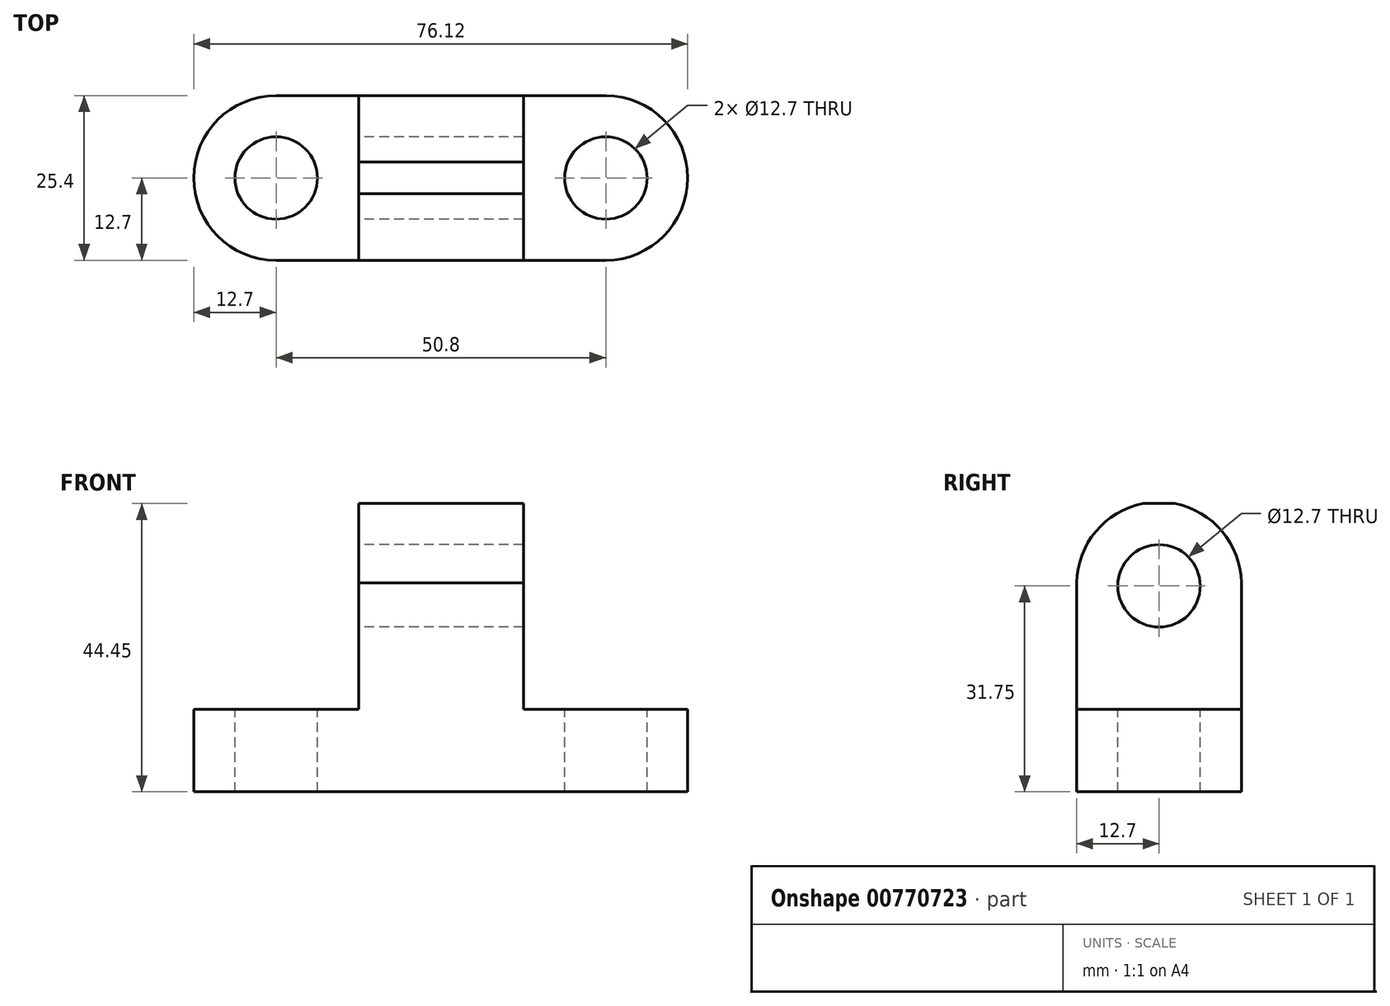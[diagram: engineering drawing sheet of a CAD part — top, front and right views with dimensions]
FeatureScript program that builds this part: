
annotation { "Feature Type Name" : "Feature", "Feature Type Description" : "" }
export const myFeature = defineFeature(function(context is Context, id is Id, definition is map)
    precondition{}
    {
        {
            var Q0;
            Q0=qCreatedBy(makeId("Front.planeOp"),FACE);
            var sketch = newSketch(context, id + "F0", { "sketchPlane" : qUnion([Q0])});
            skLineSegment(sketch, "E0.bottom", {"start": v(0, 0) * mm, "end": v(76.2, 0) * mm});
            skLineSegment(sketch, "E0.top", {"start": v(0, 12.7) * mm, "end": v(76.2, 12.7) * mm});
            skLineSegment(sketch, "E0.left", {"start": v(0, 0) * mm, "end": v(0, 12.7) * mm});
            skLineSegment(sketch, "E0.right", {"start": v(76.2, 0) * mm, "end": v(76.2, 12.7) * mm});
            skLineSegment(sketch, "E1.bottom", {"start": v(25.4, 0) * mm, "end": v(50.8, 0) * mm});
            skLineSegment(sketch, "E1.top", {"start": v(25.4, 44.45) * mm, "end": v(50.8, 44.45) * mm});
            skLineSegment(sketch, "E1.left", {"start": v(25.4, 0) * mm, "end": v(25.4, 44.45) * mm});
            skLineSegment(sketch, "E1.right", {"start": v(50.8, 0) * mm, "end": v(50.8, 44.45) * mm});
            skSolve(sketch);
        }
        {
            var Q0;
            {var subQ3=sQuery(id+"F0.wireOp",EDGE,"E0.left");Q0=makeQuery(id+"F0.imprint","IMPRINT",FACE,{"disambiguationData":[TD([[makeQuery(id+"F0.imprint","IMPRINT",EDGE,{"derivedFrom":subQ3}),-1.0]])]});}
            var Q1;
            {var subQ0=sQuery(id+"F0.wireOp",EDGE,"E1.left");var subQ1=sQuery(id+"F0.wireOp",EDGE,"E0.bottom");var subQ2=makeQuery(id+"F0.imprint","INTERSECT",VERTEX,{"derivedFrom":[subQ1,subQ0]});Q1=makeQuery(id+"F0.imprint","IMPRINT",FACE,{"disambiguationData":[TD([[makeQuery(id+"F0.imprint","IMPRINT",EDGE,{"disambiguationData":[TD([[subQ2,-1.0]])],"derivedFrom":subQ1}),1.0]])]});}
            var Q2;
            {var subQ0=sQuery(id+"F0.wireOp",EDGE,"E0.right");Q2=makeQuery(id+"F0.imprint","IMPRINT",FACE,{"disambiguationData":[TD([[makeQuery(id+"F0.imprint","IMPRINT",EDGE,{"derivedFrom":subQ0}),1.0]])]});}
            var Q3;
            {var subQ5=sQuery(id+"F0.wireOp",EDGE,"E1.top");Q3=makeQuery(id+"F0.imprint","IMPRINT",FACE,{"disambiguationData":[TD([[makeQuery(id+"F0.imprint","IMPRINT",EDGE,{"derivedFrom":subQ5}),-1.0]])]});}
            extrude(context, id + "F1", {"entities" : qUnion([Q0, Q1, Q2, Q3]), "depth" : 25.4 * mm});
        }
        {
            var Q0;
            Q0=makeQuery(id+"F1.opExtrude","SWEPT_FACE",FACE,{"disambiguationData":[OSD([sQuery(id+"F0.wireOp",EDGE,"E1.left")])]});
            var sketch = newSketch(context, id + "F2", { "sketchPlane" : qUnion([Q0])});
            skCircle(sketch, "E2", {"center": v(12.7, 31.75) * mm, "radius": 6.35 * mm});
            skArc(sketch, "E3", {"start": v(25.4, 31.75) * mm, "mid": v(12.7, 44.69) * mm, "end": v(0, 31.75) * mm});
            skSolve(sketch);
        }
        {
            var Q0;
            Q0=makeQuery(id+"F2.imprint","IMPRINT",FACE,{"disambiguationData":[TD([[makeQuery(id+"F2.imprint","IMPRINT",EDGE,{"derivedFrom":sQuery(id+"F2.wireOp",EDGE,"E2")}),1.0]])]});
            var Q1;
            {var subQ0=sQuery(id+"F2.wireOp",EDGE,"E3");var subQ1=sQuery(id+"F0.wireOp",EDGE,"E1.left");var subQ4=makeQuery(id+"F1.opExtrude","CAP_EDGE",EDGE,{"disambiguationData":[OSD([subQ1])],"isStart":true});var subQ5=makeQuery(id+"F2.imprint","INTERSECT",VERTEX,{"disambiguationData":[OD(1.0)],"derivedFrom":[subQ4,subQ0]});Q1=makeQuery(id+"F2.imprint","IMPRINT",FACE,{"disambiguationData":[TD([[makeQuery(id+"F2.imprint","IMPRINT",EDGE,{"disambiguationData":[TD([[subQ5,1.0]])],"derivedFrom":subQ0}),-1.0]])]});}
            var Q2;
            {var subQ0=sQuery(id+"F2.wireOp",EDGE,"E3");var subQ1=sQuery(id+"F0.wireOp",EDGE,"E1.left");var subQ2=makeQuery(id+"F1.opExtrude","CAP_EDGE",EDGE,{"disambiguationData":[OSD([subQ1])],"isStart":false});var subQ3=makeQuery(id+"F2.imprint","INTERSECT",VERTEX,{"disambiguationData":[OD(1.0)],"derivedFrom":[subQ2,subQ0]});Q2=makeQuery(id+"F2.imprint","IMPRINT",FACE,{"disambiguationData":[TD([[makeQuery(id+"F2.imprint","IMPRINT",EDGE,{"disambiguationData":[TD([[subQ3,-1.0]])],"derivedFrom":subQ0}),-1.0]])]});}
            extrude(context, id + "F3", {"entities" : qUnion([Q0, Q1, Q2]), "operationType" : NewBodyOperationType.REMOVE, "oppositeDirection" : true, "depth" : 25.4 * mm});
        }
        {
            var Q0;
            {var subQ0=sQuery(id+"F0.wireOp",EDGE,"E0.top");Q0=makeQuery(id+"F1.opExtrude","SWEPT_FACE",FACE,{"disambiguationData":[OSD([subQ0]),TDD([makeQuery(id+"F0.imprint","IMPRINT",EDGE,{"disambiguationData":[TD([[makeQuery(id+"F0.imprint","INTERSECT",VERTEX,{"derivedFrom":[subQ0,sQuery(id+"F0.wireOp",EDGE,"E1.left")]}),1.0]])],"derivedFrom":subQ0})])]});}
            var sketch = newSketch(context, id + "F4", { "sketchPlane" : qUnion([Q0])});
            skCircle(sketch, "E4", {"center": v(12.7, -12.7) * mm, "radius": 6.35 * mm});
            skPoint(sketch, "E4.centerSnap0", {"position": v(0, -12.7) * mm});
            skCircle(sketch, "E5", {"center": v(63.5, -12.7) * mm, "radius": 6.35 * mm});
            skArc(sketch, "E6", {"start": v(12.7, 0) * mm, "mid": v(0, -12.7) * mm, "end": v(12.7, -25.4) * mm});
            skArc(sketch, "E7", {"start": v(63.5, -25.4) * mm, "mid": v(75.9, -12.7) * mm, "end": v(63.5, 0) * mm});
            skSolve(sketch);
        }
        {
            var Q0;
            Q0=makeQuery(id+"F4.imprint","IMPRINT",FACE,{"disambiguationData":[TD([[makeQuery(id+"F4.imprint","IMPRINT",EDGE,{"derivedFrom":sQuery(id+"F4.wireOp",EDGE,"E4")}),1.0]])]});
            var Q1;
            Q1=makeQuery(id+"F4.imprint","IMPRINT",FACE,{"disambiguationData":[TD([[makeQuery(id+"F4.imprint","IMPRINT",EDGE,{"derivedFrom":sQuery(id+"F4.wireOp",EDGE,"E5")}),1.0]])]});
            var Q2;
            {var subQ0=sQuery(id+"F4.wireOp",EDGE,"E6");var subQ1=sQuery(id+"F0.wireOp",EDGE,"E0.top");var subQ2=sQuery(id+"F0.wireOp",EDGE,"E0.left");var subQ5=makeQuery(id+"F1.opExtrude","SWEPT_EDGE",EDGE,{"disambiguationData":[OSD([subQ1,subQ2])]});var subQ6=makeQuery(id+"F4.imprint","INTERSECT",VERTEX,{"derivedFrom":[subQ5,subQ0]});Q2=makeQuery(id+"F4.imprint","IMPRINT",FACE,{"disambiguationData":[TD([[makeQuery(id+"F4.imprint","IMPRINT",EDGE,{"disambiguationData":[TD([[subQ6,1.0]])],"derivedFrom":subQ0}),-1.0]])]});}
            var Q3;
            {var subQ0=sQuery(id+"F4.wireOp",EDGE,"E6");var subQ1=sQuery(id+"F0.wireOp",EDGE,"E0.top");var subQ2=sQuery(id+"F0.wireOp",EDGE,"E0.left");var subQ5=makeQuery(id+"F1.opExtrude","SWEPT_EDGE",EDGE,{"disambiguationData":[OSD([subQ1,subQ2])]});var subQ6=makeQuery(id+"F4.imprint","INTERSECT",VERTEX,{"derivedFrom":[subQ5,subQ0]});Q3=makeQuery(id+"F4.imprint","IMPRINT",FACE,{"disambiguationData":[TD([[makeQuery(id+"F4.imprint","IMPRINT",EDGE,{"disambiguationData":[TD([[subQ6,-1.0]])],"derivedFrom":subQ0}),-1.0]])]});}
            extrude(context, id + "F5", {"entities" : qUnion([Q0, Q1, Q2, Q3]), "operationType" : NewBodyOperationType.REMOVE, "oppositeDirection" : true, "depth" : 25.4 * mm});
        }
        {
            var Q0;
            {var subQ0=sQuery(id+"F0.wireOp",EDGE,"E0.top");Q0=makeQuery(id+"F1.opExtrude","SWEPT_FACE",FACE,{"disambiguationData":[OSD([subQ0]),TDD([makeQuery(id+"F0.imprint","IMPRINT",EDGE,{"disambiguationData":[TD([[makeQuery(id+"F0.imprint","INTERSECT",VERTEX,{"derivedFrom":[subQ0,sQuery(id+"F0.wireOp",EDGE,"E1.right")]}),-1.0]])],"derivedFrom":subQ0})])]});}
            var sketch = newSketch(context, id + "F6", { "sketchPlane" : qUnion([Q0])});
            skArc(sketch, "E8", {"start": v(63.5, -25.4) * mm, "mid": v(76.12, -12.7) * mm, "end": v(63.5, 0) * mm});
            skSolve(sketch);
        }
        {
            var Q0;
            {var subQ0=sQuery(id+"F6.wireOp",EDGE,"E8");Q0=makeQuery(id+"F6.imprint","IMPRINT",FACE,{"disambiguationData":[TD([[makeQuery(id+"F6.imprint","IMPRINT",EDGE,{"derivedFrom":subQ0}),-1.0]])]});}
            extrude(context, id + "F7", {"entities" : qUnion([Q0]), "operationType" : NewBodyOperationType.REMOVE, "oppositeDirection" : true, "depth" : 25.4 * mm});
        }
    });
